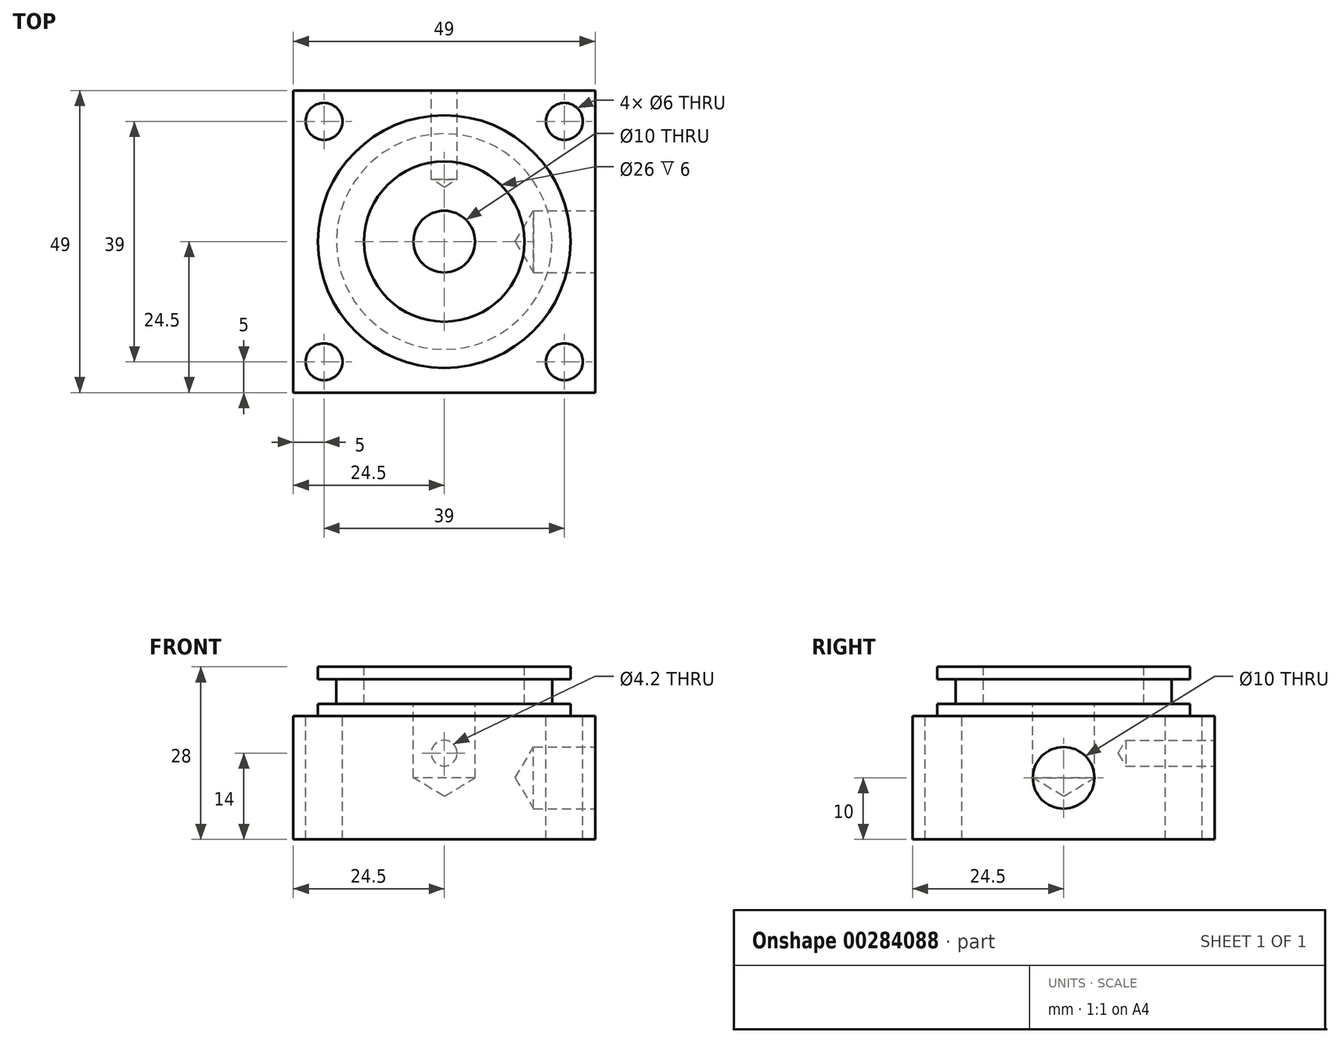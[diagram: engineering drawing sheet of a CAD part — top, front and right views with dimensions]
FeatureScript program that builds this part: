
annotation { "Feature Type Name" : "Feature", "Feature Type Description" : "" }
export const myFeature = defineFeature(function(context is Context, id is Id, definition is map)
    precondition{}
    {
        {
            var Q0;
            Q0=qCreatedBy(makeId("Top.planeOp"),FACE);
            var sketch = newSketch(context, id + "F0", { "sketchPlane" : qUnion([Q0])});
            skLineSegment(sketch, "E0.bottom", {"start": v(24.5, -24.5) * mm, "end": v(-24.5, -24.5) * mm});
            skLineSegment(sketch, "E0.top", {"start": v(24.5, 24.5) * mm, "end": v(-24.5, 24.5) * mm});
            skLineSegment(sketch, "E0.left", {"start": v(24.5, -24.5) * mm, "end": v(24.5, 24.5) * mm});
            skLineSegment(sketch, "E0.right", {"start": v(-24.5, -24.5) * mm, "end": v(-24.5, 24.5) * mm});
            skPoint(sketch, "E0.middle", {"position": v(0, 0) * mm});
            skSolve(sketch);
        }
        {
            var Q0;
            Q0=qSketchRegion(id+"F0",true);
            extrude(context, id + "F1", {"entities" : qUnion([Q0]), "depth" : 20 * mm});
        }
        {
            var Q0;
            Q0=makeQuery(id+"F1.opExtrude","CAP_FACE",FACE,{"disambiguationData":[OSD([sQuery(id+"F0.wireOp",EDGE,"E0.bottom"),sQuery(id+"F0.wireOp",EDGE,"E0.top"),sQuery(id+"F0.wireOp",EDGE,"E0.left"),sQuery(id+"F0.wireOp",EDGE,"E0.right")])],"isStart":false});
            var sketch = newSketch(context, id + "F2", { "sketchPlane" : qUnion([Q0])});
            skLineSegment(sketch, "E1.bottom", {"start": v(19.5, 19.5) * mm, "end": v(-19.5, 19.5) * mm, "construction": true});
            skLineSegment(sketch, "E1.top", {"start": v(19.5, -19.5) * mm, "end": v(-19.5, -19.5) * mm, "construction": true});
            skLineSegment(sketch, "E1.left", {"start": v(19.5, 19.5) * mm, "end": v(19.5, -19.5) * mm, "construction": true});
            skLineSegment(sketch, "E1.right", {"start": v(-19.5, 19.5) * mm, "end": v(-19.5, -19.5) * mm, "construction": true});
            skPoint(sketch, "E1.middle", {"position": v(0, 0) * mm});
            skPoint(sketch, "E2", {"position": v(-19.5, -19.5) * mm});
            skPoint(sketch, "E3", {"position": v(-19.5, 19.5) * mm});
            skPoint(sketch, "E4", {"position": v(19.5, 19.5) * mm});
            skPoint(sketch, "E5", {"position": v(19.5, -19.5) * mm});
            skSolve(sketch);
        }
        {
            var Q0;
            Q0=sQuery(id+"F2.wireOp",VERTEX,"E2");
            var Q1;
            Q1=sQuery(id+"F2.wireOp",VERTEX,"E3");
            var Q2;
            Q2=sQuery(id+"F2.wireOp",VERTEX,"E4");
            var Q3;
            Q3=sQuery(id+"F2.wireOp",VERTEX,"E5");
            var Q4;
            Q4=makeQuery(id+"F1.opExtrude","SWEPT_BODY",BODY,{"disambiguationData":[OSD([sQuery(id+"F0.wireOp",EDGE,"E0.bottom"),sQuery(id+"F0.wireOp",EDGE,"E0.top"),sQuery(id+"F0.wireOp",EDGE,"E0.left"),sQuery(id+"F0.wireOp",EDGE,"E0.right")])]});
            hole(context, id + "F3", {"style" : HoleStyle.SIMPLE, "endStyle" : HoleEndStyle.THROUGH, "holeDiameter" : 6 * mm, "tappedDepth" : 12 * mm, "tapClearance" : 3, "locations" : qUnion([Q0, Q1, Q2, Q3]), "scope" : qUnion([Q4])});
        }
        {
            var Q0;
            Q0=qCreatedBy(makeId("Right.planeOp"),FACE);
            var sketch = newSketch(context, id + "F4", { "sketchPlane" : qUnion([Q0])});
            skLineSegment(sketch, "E6.0", {"start": v(-24.5, 20) * mm, "end": v(24.5, 20) * mm, "construction": true});
            skLineSegment(sketch, "E7", {"start": v(0, 20) * mm, "end": v(0, 28) * mm});
            skLineSegment(sketch, "E8", {"start": v(0, 28) * mm, "end": v(20.5, 28) * mm});
            skLineSegment(sketch, "E9", {"start": v(20.5, 28) * mm, "end": v(20.5, 26) * mm});
            skLineSegment(sketch, "E10", {"start": v(20.5, 26) * mm, "end": v(17.5, 26) * mm});
            skLineSegment(sketch, "E11", {"start": v(17.5, 26) * mm, "end": v(17.5, 22) * mm});
            skLineSegment(sketch, "E12", {"start": v(17.5, 22) * mm, "end": v(20.5, 22) * mm});
            skLineSegment(sketch, "E13", {"start": v(20.5, 22) * mm, "end": v(20.5, 20) * mm});
            skLineSegment(sketch, "E14", {"start": v(20.5, 20) * mm, "end": v(0, 20) * mm});
            skSolve(sketch);
        }
        {
            var Q0;
            Q0=qSketchRegion(id+"F4",true);
            var Q1;
            Q1=sQuery(id+"F4.wireOp",EDGE,"E7");
            revolve(context, id + "F5", {"operationType" : NewBodyOperationType.ADD, "entities" : qUnion([Q0]), "axis" : qUnion([Q1]), "revolveType" : RevolveType.FULL});
        }
        {
            var Q0;
            Q0=makeQuery(id+"F5.opRevolve","SWEPT_FACE",FACE,{"disambiguationData":[OSD([sQuery(id+"F4.wireOp",EDGE,"E8")])]});
            var sketch = newSketch(context, id + "F6", { "sketchPlane" : qUnion([Q0])});
            skCircle(sketch, "E15.0", {"center": v(0, 0) * mm, "radius": 20.5 * mm, "construction": true});
            skSolve(sketch);
        }
        {
            var Q0;
            Q0=sQuery(id+"F6.wireOp",VERTEX,"E15.0.center");
            var Q1;
            Q1=makeQuery(id+"F1.opExtrude","SWEPT_BODY",BODY,{"disambiguationData":[OSD([sQuery(id+"F0.wireOp",EDGE,"E0.bottom"),sQuery(id+"F0.wireOp",EDGE,"E0.top"),sQuery(id+"F0.wireOp",EDGE,"E0.left"),sQuery(id+"F0.wireOp",EDGE,"E0.right")])]});
            hole(context, id + "F7", {"style" : HoleStyle.C_BORE, "endStyle" : HoleEndStyle.BLIND, "holeDiameter" : 10 * mm, "cBoreDiameter" : 26 * mm, "cBoreDepth" : 6 * mm, "holeDepth" : 18 * mm, "tappedDepth" : 12 * mm, "tapClearance" : 3, "locations" : qUnion([Q0]), "scope" : qUnion([Q1])});
        }
        {
            var Q0;
            Q0=makeQuery(id+"F1.opExtrude","SWEPT_FACE",FACE,{"disambiguationData":[OSD([sQuery(id+"F0.wireOp",EDGE,"E0.top")])]});
            var sketch = newSketch(context, id + "F8", { "sketchPlane" : qUnion([Q0])});
            skLineSegment(sketch, "E16.0", {"start": v(-24.5, 20) * mm, "end": v(24.5, 20) * mm, "construction": true});
            skLineSegment(sketch, "E17.0", {"start": v(-24.5, 0) * mm, "end": v(24.5, 0) * mm, "construction": true});
            skLineSegment(sketch, "E18", {"start": v(0, 20) * mm, "end": v(0, 14) * mm, "construction": true});
            skPoint(sketch, "E18.endSnap0", {"position": v(0, 20) * mm});
            skPoint(sketch, "E19", {"position": v(0, 14) * mm});
            skSolve(sketch);
        }
        {
            var Q0;
            Q0=sQuery(id+"F8.wireOp",VERTEX,"E19");
            var Q1;
            Q1=makeQuery(id+"F1.opExtrude","SWEPT_BODY",BODY,{"disambiguationData":[OSD([sQuery(id+"F0.wireOp",EDGE,"E0.bottom"),sQuery(id+"F0.wireOp",EDGE,"E0.top"),sQuery(id+"F0.wireOp",EDGE,"E0.left"),sQuery(id+"F0.wireOp",EDGE,"E0.right")])]});
            hole(context, id + "F9", {"style" : HoleStyle.SIMPLE, "endStyle" : HoleEndStyle.BLIND, "standardTappedOrClearance" : lookupTablePath({ "standard" : "ISO", "engagement" : "75%", "pitch" : "0.8 mm", "size" : "M5", "type" : "Tapped" }), "standardBlindInLast" : lookupTablePath({ "standard" : "ISO", "engagement" : "75%", "pitch" : "0.8 mm", "size" : "M5", "type" : "Tapped" }), "holeDiameter" : 4.2 * mm, "showTappedDepth" : true, "holeDepth" : 14.4 * mm, "tappedDepth" : 12 * mm, "tapClearance" : 3, "locations" : qUnion([Q0]), "scope" : qUnion([Q1]), "majorDiameter" : 5 * mm});
        }
        {
            var Q0;
            Q0=makeQuery(id+"F1.opExtrude","SWEPT_FACE",FACE,{"disambiguationData":[OSD([sQuery(id+"F0.wireOp",EDGE,"E0.left")])]});
            var sketch = newSketch(context, id + "F10", { "sketchPlane" : qUnion([Q0])});
            skLineSegment(sketch, "E20.0", {"start": v(-24.5, 20) * mm, "end": v(24.5, 20) * mm, "construction": true});
            skLineSegment(sketch, "E21.0", {"start": v(-24.5, 0) * mm, "end": v(24.5, 0) * mm, "construction": true});
            skLineSegment(sketch, "E22.0", {"start": v(24.5, 20) * mm, "end": v(24.5, 0) * mm, "construction": true});
            skLineSegment(sketch, "E23", {"start": v(0, 20) * mm, "end": v(0, 0) * mm, "construction": true});
            skPoint(sketch, "E24", {"position": v(0, 10) * mm});
            skSolve(sketch);
        }
        {
            var Q0;
            Q0=sQuery(id+"F10.wireOp",VERTEX,"E24");
            var Q1;
            Q1=makeQuery(id+"F1.opExtrude","SWEPT_BODY",BODY,{"disambiguationData":[OSD([sQuery(id+"F0.wireOp",EDGE,"E0.bottom"),sQuery(id+"F0.wireOp",EDGE,"E0.top"),sQuery(id+"F0.wireOp",EDGE,"E0.left"),sQuery(id+"F0.wireOp",EDGE,"E0.right")])]});
            hole(context, id + "F11", {"style" : HoleStyle.SIMPLE, "endStyle" : HoleEndStyle.BLIND, "holeDiameter" : 10 * mm, "holeDepth" : 10 * mm, "tappedDepth" : 12 * mm, "tapClearance" : 3, "locations" : qUnion([Q0]), "scope" : qUnion([Q1])});
        }
    });
